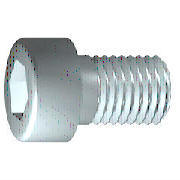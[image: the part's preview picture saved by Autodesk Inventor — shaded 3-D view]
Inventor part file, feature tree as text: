
AUTODESK INVENTOR PART (.ipt)
format: ipt  version: 2013 (Build 170138000, 138)  size: 191,488 bytes
history: native  units: mm (DEFAULTED — no unit token found)
features: sketch x2, extrude x1, plane x1, fillet x1
ambient origin geometry x7: Origin, YZ Plane, XY Plane, X Axis, Y Axis, Z Axis, Center Point
bodies: Solid1 (feature_tree), Body (feature_tree)
feature tree (5):
  extrude  "Slot"  Depth=0.306825mm
  plane  "Work Plane1"
  fillet  "Fillet2"  Radius=3.0mm
  sketch  "Sketch1"  dims[d1=13.0mm d2=0.306825mm d3=3.0mm]
  sketch  "Sketch2"  dims[d4=1.5mm d5=60.0deg d6=3.0mm d7=3.0mm d8=2.886751mm d9=5.5mm d10=90.0deg d11=10.0mm d12=0.0mm d13=13.0mm d14=0.0mm d15=0.306725mm d16=0.306725mm d17=0.3mm d19=0.0mm d26=14.0mm d27=45.0deg d28=0.0mm d29=0.0mm d30=0.1mm]
